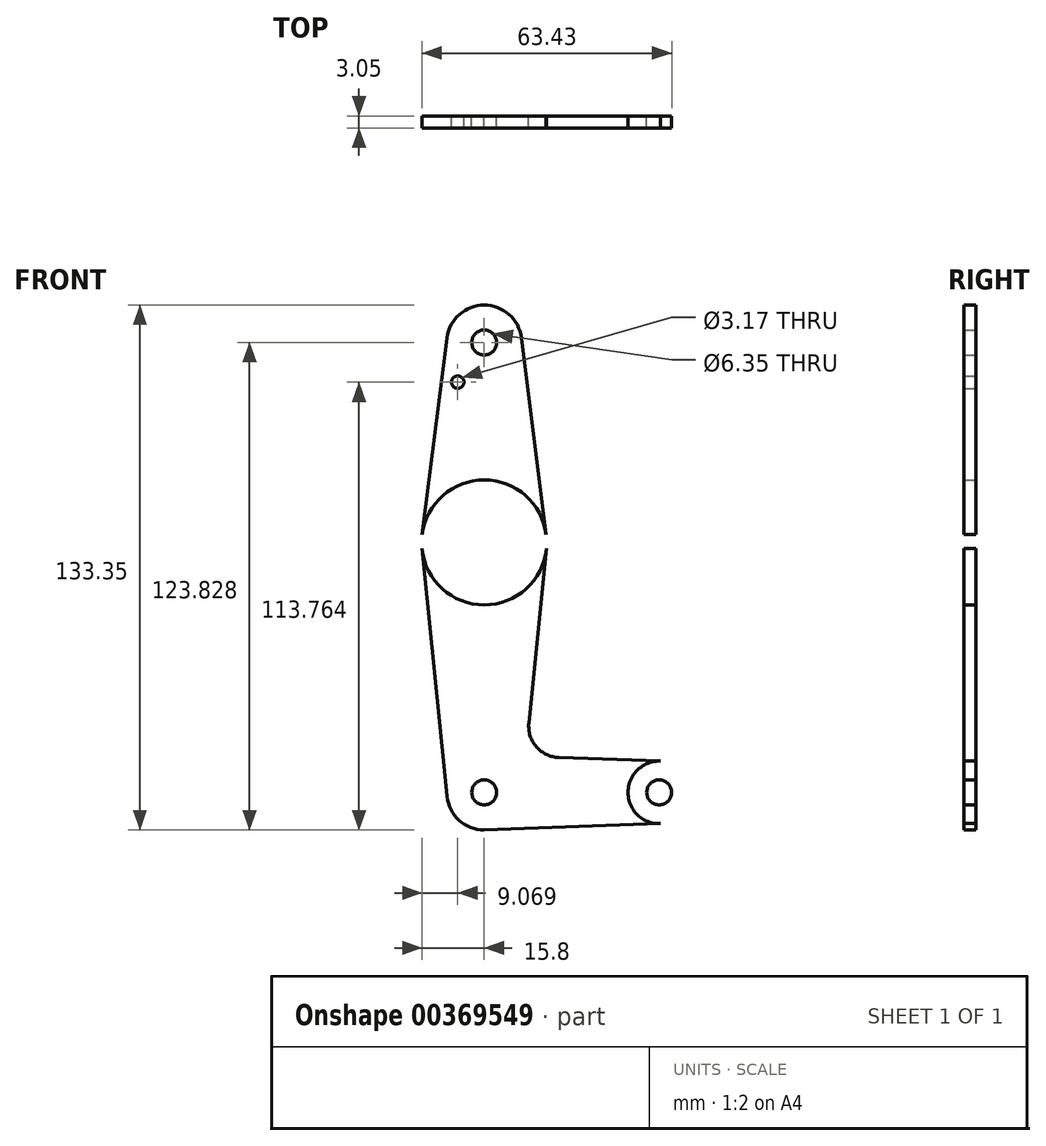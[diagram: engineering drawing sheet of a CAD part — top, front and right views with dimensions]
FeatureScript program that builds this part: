
annotation { "Feature Type Name" : "Feature", "Feature Type Description" : "" }
export const myFeature = defineFeature(function(context is Context, id is Id, definition is map)
    precondition{}
    {
        {
            var Q0;
            Q0=qCreatedBy(makeId("Front.planeOp"),FACE);
            var sketch = newSketch(context, id + "F0", { "sketchPlane" : qUnion([Q0])});
            skLineSegment(sketch, "E0", {"start": v(0, 64.52) * mm, "end": v(0, -49.78) * mm});
            skLineSegment(sketch, "E1", {"start": v(0, -49.78) * mm, "end": v(44.45, -49.78) * mm});
            skCircle(sketch, "E2", {"center": v(0, 64.52) * mm, "radius": 9.53 * mm});
            skCircle(sketch, "E3", {"center": v(0, 13.72) * mm, "radius": 15.88 * mm});
            skCircle(sketch, "E4", {"center": v(0, -49.78) * mm, "radius": 9.53 * mm});
            skCircle(sketch, "E5", {"center": v(44.45, -49.78) * mm, "radius": 7.94 * mm});
            skLineSegment(sketch, "E6", {"start": v(-9.45, 65.7) * mm, "end": v(-15.75, 15.7) * mm});
            skLineSegment(sketch, "E7", {"start": v(-15.8, 12.13) * mm, "end": v(-9.48, -50.73) * mm});
            skLineSegment(sketch, "E8", {"start": v(15.8, 12.13) * mm, "end": v(11.34, -32.19) * mm});
            skLineSegment(sketch, "E9", {"start": v(9.45, 65.7) * mm, "end": v(15.75, 15.7) * mm});
            skLineSegment(sketch, "E10", {"start": v(18.97, -40.93) * mm, "end": v(44.73, -41.85) * mm});
            skLineSegment(sketch, "E11", {"start": v(0, -59.3) * mm, "end": v(44.73, -57.71) * mm});
            skCircle(sketch, "E12", {"center": v(0, 64.52) * mm, "radius": 3.18 * mm});
            skCircle(sketch, "E13", {"center": v(-6.73, 54.45) * mm, "radius": 1.59 * mm});
            skCircle(sketch, "E14", {"center": v(0, 13.72) * mm, "radius": 3.18 * mm});
            skCircle(sketch, "E15", {"center": v(0, -49.78) * mm, "radius": 3.18 * mm});
            skCircle(sketch, "E16", {"center": v(44.45, -49.78) * mm, "radius": 3.18 * mm});
            skArc(sketch, "E17.filletArc", {"start": v(11.34, -32.19) * mm, "mid": v(13.26, -38.21) * mm, "end": v(18.97, -40.93) * mm});
            skSolve(sketch);
        }
        {
            var Q0;
            Q0=makeQuery(id+"F0.imprint","IMPRINT",FACE,{"disambiguationData":[TD([[makeQuery(id+"F0.imprint","IMPRINT",EDGE,{"derivedFrom":sQuery(id+"F0.wireOp",EDGE,"E12")}),-1.0]])]});
            var Q1;
            {var subQ5=sQuery(id+"F0.wireOp",EDGE,"E9");Q1=makeQuery(id+"F0.imprint","IMPRINT",FACE,{"disambiguationData":[TD([[makeQuery(id+"F0.imprint","IMPRINT",EDGE,{"derivedFrom":subQ5}),-1.0]])]});}
            var Q2;
            {var subQ0=sQuery(id+"F0.wireOp",EDGE,"E6");Q2=makeQuery(id+"F0.imprint","IMPRINT",FACE,{"disambiguationData":[TD([[makeQuery(id+"F0.imprint","IMPRINT",EDGE,{"derivedFrom":subQ0}),1.0]])]});}
            var Q3;
            {var subQ0=sQuery(id+"F0.wireOp",EDGE,"E3");var subQ3=sQuery(id+"F0.wireOp",EDGE,"E0");var subQ4=makeQuery(id+"F0.imprint","INTERSECT",VERTEX,{"disambiguationData":[OD(0.0)],"derivedFrom":[subQ3,subQ0]});Q3=makeQuery(id+"F0.imprint","IMPRINT",FACE,{"disambiguationData":[TD([[makeQuery(id+"F0.imprint","IMPRINT",EDGE,{"disambiguationData":[TD([[subQ4,-1.0]])],"derivedFrom":subQ3}),-1.0]])]});}
            var Q4;
            {var subQ0=sQuery(id+"F0.wireOp",EDGE,"E3");var subQ2=sQuery(id+"F0.wireOp",EDGE,"E0");var subQ5=makeQuery(id+"F0.imprint","INTERSECT",VERTEX,{"disambiguationData":[OD(0.0)],"derivedFrom":[subQ2,subQ0]});Q4=makeQuery(id+"F0.imprint","IMPRINT",FACE,{"disambiguationData":[TD([[makeQuery(id+"F0.imprint","IMPRINT",EDGE,{"disambiguationData":[TD([[subQ5,-1.0]])],"derivedFrom":subQ2}),1.0]])]});}
            var Q5;
            {var subQ5=sQuery(id+"F0.wireOp",EDGE,"E7");Q5=makeQuery(id+"F0.imprint","IMPRINT",FACE,{"disambiguationData":[TD([[makeQuery(id+"F0.imprint","IMPRINT",EDGE,{"derivedFrom":subQ5}),1.0]])]});}
            var Q6;
            {var subQ0=sQuery(id+"F0.wireOp",EDGE,"E8");Q6=makeQuery(id+"F0.imprint","IMPRINT",FACE,{"disambiguationData":[TD([[makeQuery(id+"F0.imprint","IMPRINT",EDGE,{"derivedFrom":subQ0}),-1.0]])]});}
            var Q7;
            {var subQ0=sQuery(id+"F0.wireOp",EDGE,"E4");var subQ1=sQuery(id+"F0.wireOp",EDGE,"E0");var subQ2=makeQuery(id+"F0.imprint","INTERSECT",VERTEX,{"derivedFrom":[subQ1,subQ0]});Q7=makeQuery(id+"F0.imprint","IMPRINT",FACE,{"disambiguationData":[TD([[makeQuery(id+"F0.imprint","IMPRINT",EDGE,{"disambiguationData":[TD([[subQ2,-1.0]])],"derivedFrom":subQ1}),1.0]])]});}
            var Q8;
            {var subQ0=sQuery(id+"F0.wireOp",EDGE,"E4");var subQ9=sQuery(id+"F0.wireOp",EDGE,"E0");var subQ10=makeQuery(id+"F0.imprint","INTERSECT",VERTEX,{"derivedFrom":[subQ9,subQ0]});Q8=makeQuery(id+"F0.imprint","IMPRINT",FACE,{"disambiguationData":[TD([[makeQuery(id+"F0.imprint","IMPRINT",EDGE,{"disambiguationData":[TD([[subQ10,-1.0]])],"derivedFrom":subQ9}),-1.0]])]});}
            var Q9;
            {var subQ0=sQuery(id+"F0.wireOp",EDGE,"E5");var subQ1=sQuery(id+"F0.wireOp",EDGE,"E1");var subQ2=makeQuery(id+"F0.imprint","INTERSECT",VERTEX,{"derivedFrom":[subQ1,subQ0]});Q9=makeQuery(id+"F0.imprint","IMPRINT",FACE,{"disambiguationData":[TD([[makeQuery(id+"F0.imprint","IMPRINT",EDGE,{"disambiguationData":[TD([[subQ2,1.0]])],"derivedFrom":subQ1}),-1.0]])]});}
            var Q10;
            Q10=makeQuery(id+"F0.imprint","IMPRINT",FACE,{"disambiguationData":[TD([[makeQuery(id+"F0.imprint","IMPRINT",EDGE,{"derivedFrom":sQuery(id+"F0.wireOp",EDGE,"E16")}),-1.0]])]});
            extrude(context, id + "F1", {"entities" : qUnion([Q0, Q1, Q2, Q3, Q4, Q5, Q6, Q7, Q8, Q9, Q10]), "depth" : 3.05 * mm});
        }
    });
